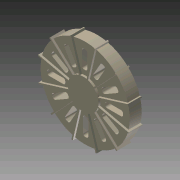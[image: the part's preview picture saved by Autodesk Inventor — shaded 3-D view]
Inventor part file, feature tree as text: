
AUTODESK INVENTOR PART (.ipt)
format: ipt  version: 2011 (Build 150239000, 239)  size: 659,968 bytes
history: native  units: in
note: dims shown in document units (in); Inventor stores cm internally (conversion verified against a paired STEP export)
features: extrude x10, sketch x10, pattern_circular x4, projected_geometry x1
ambient origin geometry x8: Origin, YZ Plane, XZ Plane, XY Plane, X Axis, Y Axis, Z Axis, Center Point
bodies: Solid1 (feature_tree)
feature tree (25):
  extrude  "Extrusion1"  Depth=3.15in
  extrude  "Extrusion2"  Depth=3.0in
  extrude  "Extrusion3"  Depth=3.375in TaperAngle=0.0deg
  extrude  "Extrusion4"  Depth=1.15in
  extrude  "Extrusion5"  Depth=0.05in
  pattern_circular  "Circular Pattern1"  Count=12 Angle=360.0deg
  extrude  "Extrusion6"  Depth=4.7244in TaperAngle=360.0deg
  pattern_circular  "Circular Pattern2"  [2 undecoded]
  extrude  "Extrusion7"  Depth=0.075in
  pattern_circular  "Circular Pattern3"  [2 undecoded]
  extrude  "Extrusion8"  Depth=4.7244in TaperAngle=360.0deg
  pattern_circular  "Circular Pattern4"  [2 undecoded]
  extrude  "Extrusion9"  Depth=0.075in
  extrude  "Extrusion10"  Depth=0.15in TaperAngle=0.0deg
  sketch  "Sketch1"  dims[d0=3.35in d1=3.15in]
  sketch  "Sketch2"  dims[d2=3.375in d3=0.0in d4=3.0in]
  sketch  "Sketch3"  dims[d5=0.125in d6=0.0in d7=3.375in d8=0.0in]
  sketch  "Sketch4"  dims[d9=0.45in d10=0.0in d11=1.15in]
  sketch  "Sketch5"  dims[d13=0.05in d15=0.05in]
  sketch  "Sketch6"  dims[d16=0.05in d18=4.7244in d20=360.0deg]
  sketch  "Sketch7"  dims[d22=0.075in d23=0.0in d24=4.7244in d25=360.0deg]
  projected_geometry  "Projected Loop1"
  sketch  "Sketch8"  dims[d27=0.1168in]
  sketch  "Sketch9"  dims[d28=0.675in]
  sketch  "Sketch10"  dims[d29=0.2in d30=0.25in d31=0.075in d32=0.45in d33=0.0in d34=4.7244in d35=360.0deg d38=0.075in d39=0.075in d40=0.15in d41=0.0in d42=4.7244in d43=360.0deg d45=3.7in d46=0.0in d47=4.7244in d48=360.0deg d50=0.07in d51=0.0in d52=1.0in d53=0.0in]
note: 6 required parameter values undecoded (feature->parameter linkage not recoverable at this tier; creation-order binding heuristic only, values carry confidence <= 0.55)
